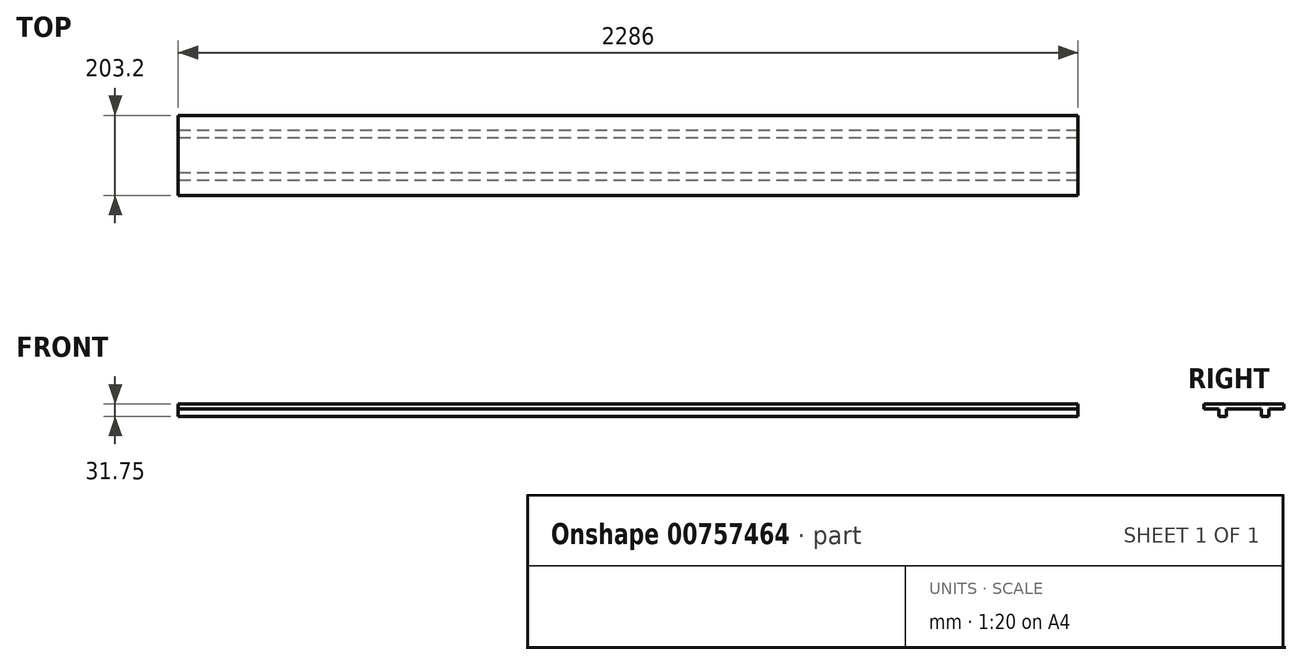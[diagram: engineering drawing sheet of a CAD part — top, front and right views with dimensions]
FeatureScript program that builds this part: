
annotation { "Feature Type Name" : "Feature", "Feature Type Description" : "" }
export const myFeature = defineFeature(function(context is Context, id is Id, definition is map)
    precondition{}
    {
        {
            var Q0;
            Q0=qCreatedBy(makeId("Right.planeOp"),FACE);
            var sketch = newSketch(context, id + "F0", { "sketchPlane" : qUnion([Q0])});
            skLineSegment(sketch, "E0", {"start": v(-101.6, 12.7) * mm, "end": v(101.6, 12.7) * mm});
            skLineSegment(sketch, "E1", {"start": v(101.6, 12.7) * mm, "end": v(101.6, 0) * mm});
            skLineSegment(sketch, "E2", {"start": v(101.6, 0) * mm, "end": v(63.5, 0) * mm});
            skLineSegment(sketch, "E3", {"start": v(63.5, 0) * mm, "end": v(63.5, -19.05) * mm});
            skLineSegment(sketch, "E4", {"start": v(63.5, -19.05) * mm, "end": v(44.45, -19.05) * mm});
            skLineSegment(sketch, "E5", {"start": v(44.45, -19.05) * mm, "end": v(44.45, 0) * mm});
            skLineSegment(sketch, "E6", {"start": v(44.45, 0) * mm, "end": v(-44.45, 0) * mm});
            skLineSegment(sketch, "E7", {"start": v(-44.45, 0) * mm, "end": v(-44.45, -19.05) * mm});
            skLineSegment(sketch, "E8", {"start": v(-44.45, -19.05) * mm, "end": v(-63.5, -19.05) * mm});
            skLineSegment(sketch, "E9", {"start": v(-63.5, -19.05) * mm, "end": v(-63.5, 0) * mm});
            skLineSegment(sketch, "E10", {"start": v(-63.5, 0) * mm, "end": v(-101.6, 0) * mm});
            skLineSegment(sketch, "E11", {"start": v(-101.6, 0) * mm, "end": v(-101.6, 12.7) * mm});
            skSolve(sketch);
        }
        {
            var Q0;
            Q0 = qSketchRegion(id + "F0", true);
            extrude(context, id + "F1", {"entities" : qUnion([Q0]), "endBound" : BoundingType.SYMMETRIC, "depth" : 2286 * mm, "offsetDistance" : 25.4 * mm});
        }
    });
